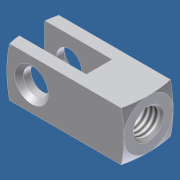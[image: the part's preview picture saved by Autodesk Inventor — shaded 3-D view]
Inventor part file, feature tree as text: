
AUTODESK INVENTOR PART (.ipt)
format: ipt  version: unknown  size: 256,000 bytes
history: native  units: in
note: dims shown in document units (in); Inventor stores cm internally (conversion verified against a paired STEP export)
features: other x126, sketch x7, revolve x5, extrude x2, thread x1
ambient origin geometry x8: Origin, YZ Plane, XZ Plane, XY Plane, X Axis, Y Axis, Z Axis, Center Point
feature tree (141):
  extrude  "Extrusion1"  Depth=0.5in TaperAngle=0.0deg
  extrude  "Extrusion2"  Depth=0.44in TaperAngle=0.0deg
  revolve  "Revolution1"  Angle=360.0deg
  thread  "Thread1"  [1 undecoded]
  revolve  "Revolution2"  [1 undecoded]
  revolve  "Revolution3"  [1 undecoded]
  revolve  "Revolution4"  [1 undecoded]
  revolve  "Revolution5"  [1 undecoded]
  other  "th1_XY"
  other  "th1_YZ"
  other  "th1_ZX"
  other  "th1_X"
  other  "th1_Y"
  other  "th1_Z"
  other  "th1_Center"
  other  "th2_XY"
  other  "th2_YZ"
  other  "th2_ZX"
  other  "th2_X"
  other  "th2_Y"
  other  "th2_Z"
  other  "th2_Center"
  other  "rod_clevis_body_XY"
  other  "rod_clevis_body_YZ"
  other  "rod_clevis_body_ZX"
  other  "rod_clevis_body_X"
  other  "rod_clevis_body_Y"
  other  "rod_clevis_body_Z"
  other  "rod_clevis_body_Center"
  other  "piston_rod_clevis_XY"
  other  "piston_rod_clevis_YZ"
  other  "piston_rod_clevis_ZX"
  other  "piston_rod_clevis_X"
  other  "piston_rod_clevis_Y"
  other  "piston_rod_clevis_Z"
  other  "piston_rod_clevis_Center"
  other  "dummy_XY"
  other  "dummy_YZ"
  other  "dummy_ZX"
  other  "dummy_X"
  other  "dummy_Y"
  other  "dummy_Z"
  other  "dummy_Center"
  other  "l11_XY"
  other  "l11_YZ"
  other  "l11_ZX"
  other  "l11_X"
  other  "l11_Y"
  other  "l11_Z"
  other  "l11_Center"
  other  "l12_XY"
  other  "l12_YZ"
  other  "l12_ZX"
  other  "l12_X"
  other  "l12_Y"
  other  "l12_Z"
  other  "l12_Center"
  other  "l1_XY"
  other  "l1_YZ"
  other  "l1_ZX"
  other  "l1_X"
  other  "l1_Y"
  other  "l1_Z"
  other  "l1_Center"
  other  "h1_XY"
  other  "h1_YZ"
  other  "h1_ZX"
  other  "h1_X"
  other  "h1_Y"
  other  "h1_Z"
  other  "h1_Center"
  other  "l2_XY"
  other  "l2_YZ"
  other  "l2_ZX"
  other  "l2_X"
  other  "l2_Y"
  other  "l2_Z"
  other  "l2_Center"
  other  "h2_XY"
  other  "h2_YZ"
  other  "h2_ZX"
  other  "h2_X"
  other  "h2_Y"
  other  "h2_Z"
  other  "h2_Center"
  other  "w11_XY"
  other  "w11_YZ"
  other  "w11_ZX"
  other  "w11_X"
  other  "w11_Y"
  other  "w11_Z"
  other  "w11_Center"
  other  "w12_XY"
  other  "w12_YZ"
  other  "w12_ZX"
  other  "w12_X"
  other  "w12_Y"
  other  "w12_Z"
  other  "w12_Center"
  other  "l21_XY"
  other  "l21_YZ"
  other  "l21_ZX"
  other  "l21_X"
  other  "l21_Y"
  other  "l21_Z"
  other  "l21_Center"
  other  "l22_XY"
  other  "l22_YZ"
  other  "l22_ZX"
  other  "l22_X"
  other  "l22_Y"
  other  "l22_Z"
  other  "l22_Center"
  other  "w1_XY"
  other  "w1_YZ"
  other  "w1_ZX"
  other  "w1_X"
  other  "w1_Y"
  other  "w1_Z"
  other  "w1_Center"
  other  "w2_XY"
  other  "w2_YZ"
  other  "w2_ZX"
  other  "w2_X"
  other  "w2_Y"
  other  "w2_Z"
  other  "w2_Center"
  other  "to_cylinder_XY"
  other  "to_cylinder_YZ"
  other  "to_cylinder_ZX"
  other  "to_cylinder_X"
  other  "to_cylinder_Y"
  other  "to_cylinder_Z"
  other  "to_cylinder_Center"
  sketch  "Sketch_1"  dims[d0=0.5in d1=0.0in d2=0.5in d3=0.0in]
  sketch  "Sketch_2"  dims[d4=360.0deg d5=0.44in d6=0.0in]
  sketch  "Sketch_3"  dims[d7=360.0deg d8=360.0deg d9=360.0deg]
  sketch  "Sketch_4"  dims[d10=360.0deg]
  sketch  "Sketch_5"
  sketch  "Sketch_9"
  sketch  "Sketch_10"
note: 5 required parameter values undecoded (feature->parameter linkage not recoverable at this tier; creation-order binding heuristic only, values carry confidence <= 0.55)
